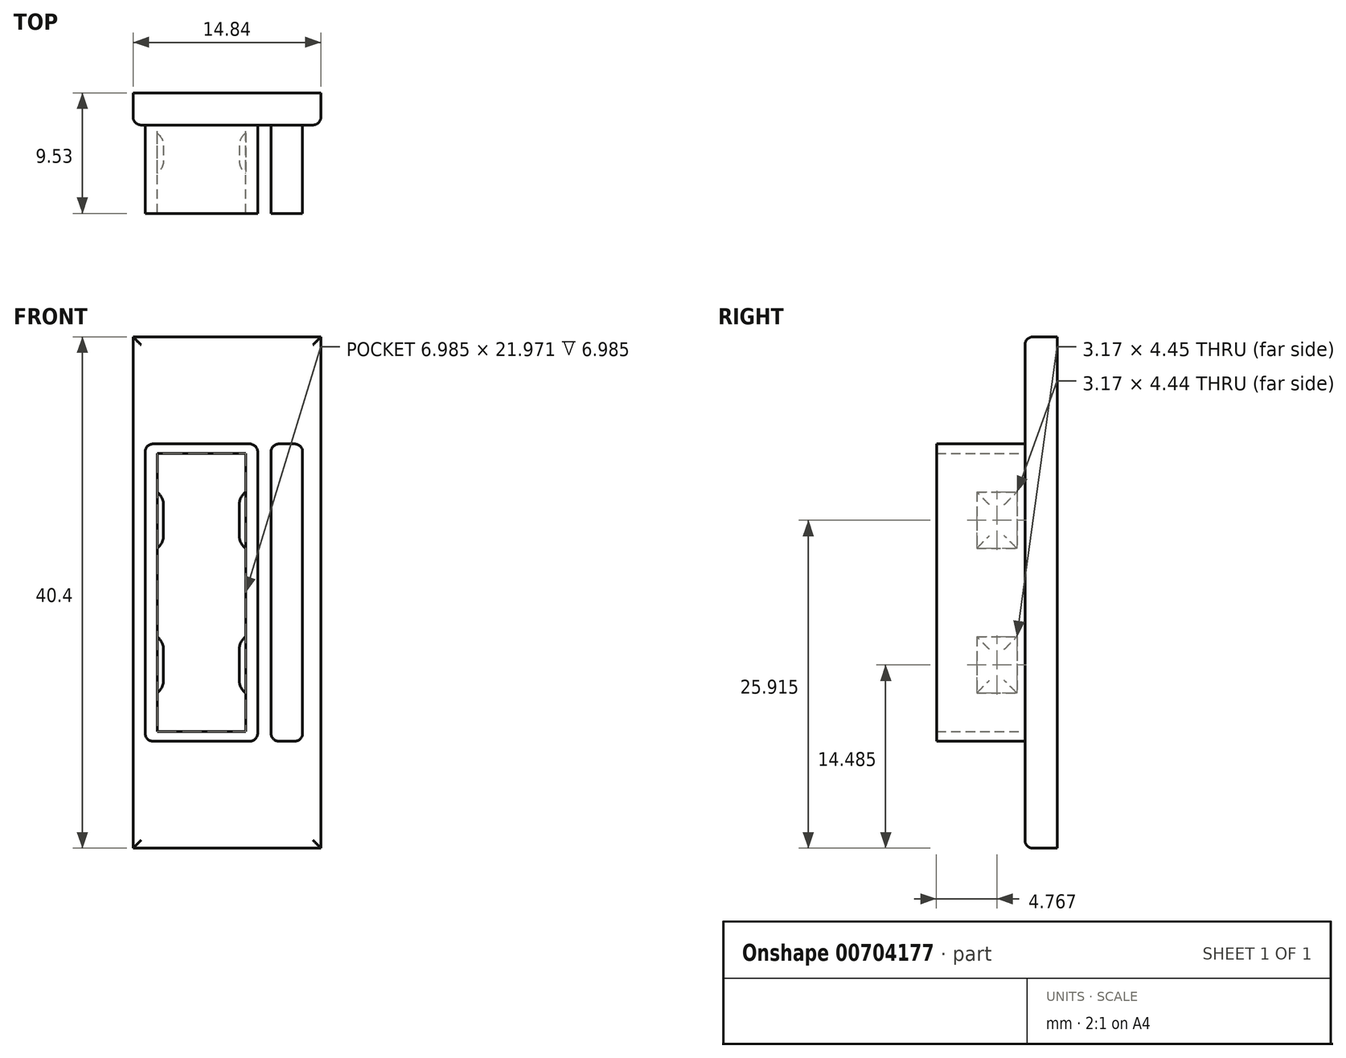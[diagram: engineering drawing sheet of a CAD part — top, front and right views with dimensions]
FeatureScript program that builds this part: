
annotation { "Feature Type Name" : "Feature", "Feature Type Description" : "" }
export const myFeature = defineFeature(function(context is Context, id is Id, definition is map)
    precondition{}
    {
        {
            var Q0;
            Q0=qCreatedBy(makeId("Front.planeOp"),FACE);
            var sketch = newSketch(context, id + "F0", { "sketchPlane" : qUnion([Q0])});
            skLineSegment(sketch, "E0.bottom", {"start": v(0, 0) * mm, "end": v(10.8, 0) * mm});
            skLineSegment(sketch, "E0.top", {"start": v(0, -25.4) * mm, "end": v(10.8, -25.4) * mm});
            skLineSegment(sketch, "E0.left", {"start": v(0, 0) * mm, "end": v(0, -25.4) * mm});
            skLineSegment(sketch, "E0.right", {"start": v(10.8, 0) * mm, "end": v(10.8, -25.4) * mm});
            skSolve(sketch);
        }
        {
            var Q0;
            Q0=makeQuery(id+"F0.imprint","IMPRINT",FACE,{"disambiguationData":[TD([[makeQuery(id+"F0.imprint","IMPRINT",EDGE,{"derivedFrom":sQuery(id+"F0.wireOp",EDGE,"E0.bottom")}),-1.0]])]});
            extrude(context, id + "F1", {"entities" : qUnion([Q0]), "depth" : 2.54 * mm});
        }
        {
            var Q0;
            Q0=makeQuery(id+"F1.opExtrude","CAP_FACE",FACE,{"disambiguationData":[OSD([sQuery(id+"F0.wireOp",EDGE,"E0.bottom"),sQuery(id+"F0.wireOp",EDGE,"E0.top"),sQuery(id+"F0.wireOp",EDGE,"E0.left"),sQuery(id+"F0.wireOp",EDGE,"E0.right")])],"isStart":false});
            var sketch = newSketch(context, id + "F2", { "sketchPlane" : qUnion([Q0])});
            skLineSegment(sketch, "E1.0", {"start": v(0.95, -0.95) * mm, "end": v(9.84, -0.95) * mm});
            skLineSegment(sketch, "E1.1", {"start": v(0.95, -0.95) * mm, "end": v(0.95, -24.45) * mm});
            skLineSegment(sketch, "E1.2", {"start": v(0.95, -24.45) * mm, "end": v(9.84, -24.45) * mm});
            skLineSegment(sketch, "E1.3", {"start": v(9.84, -0.95) * mm, "end": v(9.84, -24.45) * mm});
            skLineSegment(sketch, "E2.bottom", {"start": v(1.9, -1.71) * mm, "end": v(8.9, -1.71) * mm});
            skLineSegment(sketch, "E2.top", {"start": v(1.9, -23.69) * mm, "end": v(8.9, -23.69) * mm});
            skLineSegment(sketch, "E2.left", {"start": v(1.9, -1.71) * mm, "end": v(1.9, -23.69) * mm});
            skLineSegment(sketch, "E2.right", {"start": v(8.9, -1.71) * mm, "end": v(8.9, -23.69) * mm});
            skSolve(sketch);
        }
        {
            var Q0;
            Q0=makeQuery(id+"F2.imprint","IMPRINT",FACE,{"disambiguationData":[TD([[makeQuery(id+"F2.imprint","IMPRINT",EDGE,{"derivedFrom":sQuery(id+"F2.wireOp",EDGE,"E1.0")}),-1.0]])]});
            extrude(context, id + "F3", {"entities" : qUnion([Q0]), "operationType" : NewBodyOperationType.ADD, "depth" : 7 * mm});
        }
        {
            var Q0;
            Q0=makeQuery(id+"F3.opExtrude","SWEPT_FACE",FACE,{"disambiguationData":[OSD([sQuery(id+"F2.wireOp",EDGE,"E2.left")])]});
            var sketch = newSketch(context, id + "F4", { "sketchPlane" : qUnion([Q0])});
            skLineSegment(sketch, "E3.bottom", {"start": v(-6.35, -4.76) * mm, "end": v(-3.18, -4.76) * mm});
            skLineSegment(sketch, "E3.top", {"start": v(-6.35, -9.2) * mm, "end": v(-3.18, -9.2) * mm});
            skLineSegment(sketch, "E3.left", {"start": v(-6.35, -4.76) * mm, "end": v(-6.35, -9.2) * mm});
            skLineSegment(sketch, "E3.right", {"start": v(-3.18, -4.76) * mm, "end": v(-3.18, -9.2) * mm});
            skLineSegment(sketch, "E4.bottom", {"start": v(-6.35, -16.2) * mm, "end": v(-3.18, -16.2) * mm});
            skLineSegment(sketch, "E4.top", {"start": v(-6.35, -20.64) * mm, "end": v(-3.18, -20.64) * mm});
            skLineSegment(sketch, "E4.left", {"start": v(-6.35, -16.2) * mm, "end": v(-6.35, -20.64) * mm});
            skLineSegment(sketch, "E4.right", {"start": v(-3.18, -16.2) * mm, "end": v(-3.18, -20.64) * mm});
            skSolve(sketch);
        }
        {
            var Q0;
            Q0=qSketchRegion(id+"F4",true);
            extrude(context, id + "F5", {"entities" : qUnion([Q0]), "operationType" : NewBodyOperationType.ADD, "depth" : 0.5 * mm});
        }
        {
            var Q0;
            Q0=makeQuery(id+"F3.opExtrude","SWEPT_FACE",FACE,{"disambiguationData":[OSD([sQuery(id+"F2.wireOp",EDGE,"E2.right")])]});
            var sketch = newSketch(context, id + "F6", { "sketchPlane" : qUnion([Q0])});
            skLineSegment(sketch, "E5.bottom", {"start": v(3.17, -4.76) * mm, "end": v(6.35, -4.76) * mm});
            skLineSegment(sketch, "E5.top", {"start": v(3.18, -9.2) * mm, "end": v(6.35, -9.2) * mm});
            skLineSegment(sketch, "E5.left", {"start": v(3.17, -4.76) * mm, "end": v(3.18, -9.2) * mm});
            skLineSegment(sketch, "E5.right", {"start": v(6.35, -4.76) * mm, "end": v(6.35, -9.2) * mm});
            skLineSegment(sketch, "E6.bottom", {"start": v(3.18, -16.2) * mm, "end": v(6.35, -16.2) * mm});
            skLineSegment(sketch, "E6.top", {"start": v(3.18, -20.64) * mm, "end": v(6.35, -20.64) * mm});
            skLineSegment(sketch, "E6.left", {"start": v(3.18, -16.2) * mm, "end": v(3.18, -20.64) * mm});
            skLineSegment(sketch, "E6.right", {"start": v(6.35, -16.2) * mm, "end": v(6.35, -20.64) * mm});
            skSolve(sketch);
        }
        {
            var Q0;
            Q0=qSketchRegion(id+"F6",true);
            extrude(context, id + "F7", {"entities" : qUnion([Q0]), "operationType" : NewBodyOperationType.ADD, "depth" : 0.5 * mm});
        }
        {
            var Q0;
            Q0=makeQuery(id+"F5.opExtrude","CAP_FACE",FACE,{"disambiguationData":[OSD([sQuery(id+"F4.wireOp",EDGE,"E4.bottom"),sQuery(id+"F4.wireOp",EDGE,"E4.top"),sQuery(id+"F4.wireOp",EDGE,"E4.left"),sQuery(id+"F4.wireOp",EDGE,"E4.right")])],"isStart":false});
            var Q1;
            Q1=makeQuery(id+"F5.opExtrude","CAP_FACE",FACE,{"disambiguationData":[OSD([sQuery(id+"F4.wireOp",EDGE,"E3.bottom"),sQuery(id+"F4.wireOp",EDGE,"E3.top"),sQuery(id+"F4.wireOp",EDGE,"E3.left"),sQuery(id+"F4.wireOp",EDGE,"E3.right")])],"isStart":false});
            var Q2;
            Q2=makeQuery(id+"F7.opExtrude","CAP_FACE",FACE,{"disambiguationData":[OSD([sQuery(id+"F6.wireOp",EDGE,"E5.bottom"),sQuery(id+"F6.wireOp",EDGE,"E5.top"),sQuery(id+"F6.wireOp",EDGE,"E5.left"),sQuery(id+"F6.wireOp",EDGE,"E5.right")])],"isStart":false});
            var Q3;
            Q3=makeQuery(id+"F7.opExtrude","CAP_FACE",FACE,{"disambiguationData":[OSD([sQuery(id+"F6.wireOp",EDGE,"E6.bottom"),sQuery(id+"F6.wireOp",EDGE,"E6.top"),sQuery(id+"F6.wireOp",EDGE,"E6.left"),sQuery(id+"F6.wireOp",EDGE,"E6.right")])],"isStart":false});
            fillet(context, id + "F8", {"entities" : qUnion([Q0, Q1, Q2, Q3]), "radius" : 1.27 * mm, "tangentPropagation" : true, "allowEdgeOverflow" : false});
        }
        {
            var Q0;
            Q0=qCreatedBy(makeId("Front.planeOp"),FACE);
            var sketch = newSketch(context, id + "F9", { "sketchPlane" : qUnion([Q0])});
            skLineSegment(sketch, "E7.bottom", {"start": v(0, 0) * mm, "end": v(10.8, 0) * mm});
            skLineSegment(sketch, "E7.top", {"start": v(0, 7.5) * mm, "end": v(10.8, 7.5) * mm});
            skLineSegment(sketch, "E7.left", {"start": v(0, 0) * mm, "end": v(0, 7.5) * mm});
            skLineSegment(sketch, "E7.right", {"start": v(10.8, 0) * mm, "end": v(10.8, 7.5) * mm});
            skLineSegment(sketch, "E8.bottom", {"start": v(0, -25.4) * mm, "end": v(10.8, -25.4) * mm});
            skLineSegment(sketch, "E8.top", {"start": v(0, -32.9) * mm, "end": v(10.8, -32.9) * mm});
            skLineSegment(sketch, "E8.left", {"start": v(0, -25.4) * mm, "end": v(0, -32.9) * mm});
            skLineSegment(sketch, "E8.right", {"start": v(10.8, -25.4) * mm, "end": v(10.8, -32.9) * mm});
            skLineSegment(sketch, "E9.bottom", {"start": v(10.8, 7.5) * mm, "end": v(14.84, 7.5) * mm});
            skLineSegment(sketch, "E9.top", {"start": v(10.8, -32.9) * mm, "end": v(14.84, -32.9) * mm});
            skLineSegment(sketch, "E9.left", {"start": v(10.8, 7.5) * mm, "end": v(10.8, -32.9) * mm});
            skLineSegment(sketch, "E9.right", {"start": v(14.84, 7.5) * mm, "end": v(14.84, -32.9) * mm});
            skSolve(sketch);
        }
        {
            var Q0;
            Q0 = qSketchRegion(id + "F9", true);
            extrude(context, id + "F10", {"entities" : qUnion([Q0]), "operationType" : NewBodyOperationType.ADD, "depth" : 2.54 * mm});
        }
        {
            var Q0;
            {var subQ0=sQuery(id+"F0.wireOp",EDGE,"E0.left");var subQ1=sQuery(id+"F0.wireOp",EDGE,"E0.top");var subQ2=sQuery(id+"F0.wireOp",EDGE,"E0.right");var subQ3=sQuery(id+"F0.wireOp",EDGE,"E0.bottom");Q0=makeQuery(id+"F10.boolean.opBoolean","MERGE",FACE,{"derivedFrom":[makeQuery(id+"F3.boolean.opBoolean","SPLIT",FACE,{"disambiguationData":[TD([makeQuery(id+"F1.opExtrude","SWEPT_FACE",FACE,{"disambiguationData":[OSD([subQ3])]})])],"derivedFrom":makeQuery(id+"F1.opExtrude","CAP_FACE",FACE,{"disambiguationData":[OSD([subQ3,subQ1,subQ0,subQ2])],"isStart":false})}),makeQuery(id+"F10.opExtrude","CAP_FACE",FACE,{"disambiguationData":[OSD([sQuery(id+"F9.wireOp",EDGE,"E7.bottom"),sQuery(id+"F9.wireOp",EDGE,"E7.top"),sQuery(id+"F9.wireOp",EDGE,"E7.left"),sQuery(id+"F9.wireOp",EDGE,"E8.bottom"),sQuery(id+"F9.wireOp",EDGE,"E8.top"),sQuery(id+"F9.wireOp",EDGE,"E8.left"),sQuery(id+"F9.wireOp",EDGE,"E9.bottom"),sQuery(id+"F9.wireOp",EDGE,"E9.top"),sQuery(id+"F9.wireOp",EDGE,"E9.left"),sQuery(id+"F9.wireOp",EDGE,"E9.right")])],"isStart":false})]});}
            var sketch = newSketch(context, id + "F11", { "sketchPlane" : qUnion([Q0])});
            skLineSegment(sketch, "E10.bottom", {"start": v(10.9, -0.95) * mm, "end": v(13.4, -0.95) * mm});
            skLineSegment(sketch, "E10.top", {"start": v(10.9, -24.45) * mm, "end": v(13.4, -24.45) * mm});
            skLineSegment(sketch, "E10.left", {"start": v(10.9, -0.95) * mm, "end": v(10.9, -24.45) * mm});
            skLineSegment(sketch, "E10.right", {"start": v(13.4, -0.95) * mm, "end": v(13.4, -24.45) * mm});
            skSolve(sketch);
        }
        {
            var Q0;
            Q0=makeQuery(id+"F11.imprint","IMPRINT",FACE,{"disambiguationData":[TD([[makeQuery(id+"F11.imprint","IMPRINT",EDGE,{"derivedFrom":sQuery(id+"F11.wireOp",EDGE,"E10.bottom")}),-1.0]])]});
            extrude(context, id + "F12", {"entities" : qUnion([Q0]), "operationType" : NewBodyOperationType.ADD, "depth" : 7 * mm});
        }
        {
            var Q0;
            Q0=makeQuery(id+"F3.opExtrude","SWEPT_EDGE",EDGE,{"disambiguationData":[OSD([sQuery(id+"F2.wireOp",EDGE,"E1.0"),sQuery(id+"F2.wireOp",EDGE,"E1.1")])]});
            var Q1;
            Q1=makeQuery(id+"F3.opExtrude","SWEPT_EDGE",EDGE,{"disambiguationData":[OSD([sQuery(id+"F2.wireOp",EDGE,"E1.0"),sQuery(id+"F2.wireOp",EDGE,"E1.3")])]});
            var Q2;
            Q2=makeQuery(id+"F1.opExtrude","SWEPT_EDGE",EDGE,{"disambiguationData":[OSD([sQuery(id+"F0.wireOp",EDGE,"E0.bottom"),sQuery(id+"F0.wireOp",EDGE,"E0.right")])]});
            var Q3;
            Q3=makeQuery(id+"F1.opExtrude","SWEPT_EDGE",EDGE,{"disambiguationData":[OSD([sQuery(id+"F0.wireOp",EDGE,"E0.bottom"),sQuery(id+"F0.wireOp",EDGE,"E0.left")])]});
            var Q4;
            Q4=makeQuery(id+"F3.opExtrude","SWEPT_EDGE",EDGE,{"disambiguationData":[OSD([sQuery(id+"F2.wireOp",EDGE,"E1.2"),sQuery(id+"F2.wireOp",EDGE,"E1.3")])]});
            var Q5;
            Q5=makeQuery(id+"F3.opExtrude","SWEPT_EDGE",EDGE,{"disambiguationData":[OSD([sQuery(id+"F2.wireOp",EDGE,"E1.1"),sQuery(id+"F2.wireOp",EDGE,"E1.2")])]});
            var Q6;
            Q6=makeQuery(id+"F1.opExtrude","SWEPT_EDGE",EDGE,{"disambiguationData":[OSD([sQuery(id+"F0.wireOp",EDGE,"E0.top"),sQuery(id+"F0.wireOp",EDGE,"E0.right")])]});
            var Q7;
            Q7=makeQuery(id+"F1.opExtrude","SWEPT_EDGE",EDGE,{"disambiguationData":[OSD([sQuery(id+"F0.wireOp",EDGE,"E0.top"),sQuery(id+"F0.wireOp",EDGE,"E0.left")])]});
            var Q8;
            Q8=makeQuery(id+"F1.opExtrude","CAP_EDGE",EDGE,{"disambiguationData":[OSD([sQuery(id+"F0.wireOp",EDGE,"E0.top")])],"isStart":false});
            var Q9;
            Q9=makeQuery(id+"F1.opExtrude","CAP_EDGE",EDGE,{"disambiguationData":[OSD([sQuery(id+"F0.wireOp",EDGE,"E0.left")])],"isStart":false});
            var Q10;
            Q10=makeQuery(id+"F1.opExtrude","CAP_EDGE",EDGE,{"disambiguationData":[OSD([sQuery(id+"F0.wireOp",EDGE,"E0.right")])],"isStart":false});
            var Q11;
            Q11=makeQuery(id+"F1.opExtrude","CAP_EDGE",EDGE,{"disambiguationData":[OSD([sQuery(id+"F0.wireOp",EDGE,"E0.bottom")])],"isStart":false});
            var Q12;
            Q12=makeQuery(id+"F12.opExtrude","SWEPT_EDGE",EDGE,{"disambiguationData":[OSD([sQuery(id+"F11.wireOp",EDGE,"E10.top"),sQuery(id+"F11.wireOp",EDGE,"E10.left")])]});
            var Q13;
            Q13=makeQuery(id+"F12.opExtrude","SWEPT_EDGE",EDGE,{"disambiguationData":[OSD([sQuery(id+"F11.wireOp",EDGE,"E10.top"),sQuery(id+"F11.wireOp",EDGE,"E10.right")])]});
            var Q14;
            Q14=makeQuery(id+"F12.opExtrude","SWEPT_EDGE",EDGE,{"disambiguationData":[OSD([sQuery(id+"F11.wireOp",EDGE,"E10.bottom"),sQuery(id+"F11.wireOp",EDGE,"E10.left")])]});
            var Q15;
            Q15=makeQuery(id+"F12.opExtrude","SWEPT_EDGE",EDGE,{"disambiguationData":[OSD([sQuery(id+"F11.wireOp",EDGE,"E10.bottom"),sQuery(id+"F11.wireOp",EDGE,"E10.right")])]});
            var Q16;
            Q16=makeQuery(id+"F10.opExtrude","CAP_EDGE",EDGE,{"disambiguationData":[OSD([sQuery(id+"F9.wireOp",EDGE,"E9.right")])],"isStart":false});
            var Q17;
            Q17=makeQuery(id+"F10.opExtrude","CAP_EDGE",EDGE,{"disambiguationData":[OSD([sQuery(id+"F9.wireOp",EDGE,"E8.top"),sQuery(id+"F9.wireOp",EDGE,"E9.top")])],"isStart":false});
            var Q18;
            Q18=makeQuery(id+"F10.opExtrude","CAP_EDGE",EDGE,{"disambiguationData":[OSD([sQuery(id+"F9.wireOp",EDGE,"E7.top"),sQuery(id+"F9.wireOp",EDGE,"E9.bottom")])],"isStart":false});
            fillet(context, id + "F13", {"entities" : qUnion([Q0, Q1, Q2, Q3, Q4, Q5, Q6, Q7, Q8, Q9, Q10, Q11, Q12, Q13, Q14, Q15, Q16, Q17, Q18]), "radius" : 0.64 * mm, "tangentPropagation" : true, "allowEdgeOverflow" : false});
        }
    });
